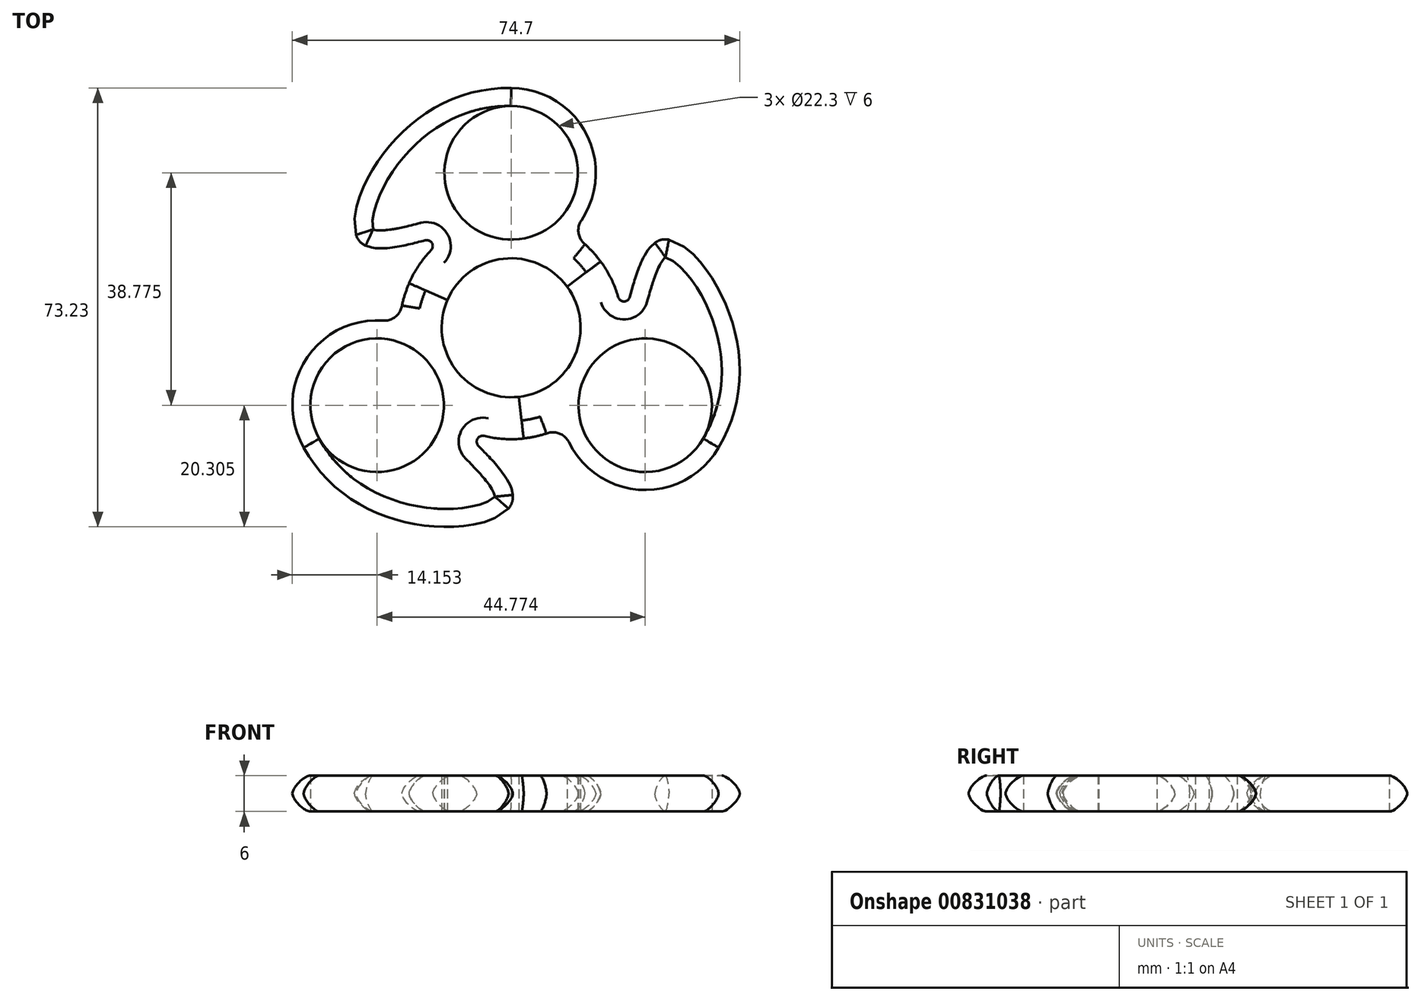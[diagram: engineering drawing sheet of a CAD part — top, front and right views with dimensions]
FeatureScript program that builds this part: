
annotation { "Feature Type Name" : "Feature", "Feature Type Description" : "" }
export const myFeature = defineFeature(function(context is Context, id is Id, definition is map)
    precondition{}
    {
        {
            var Q0;
            Q0=qCreatedBy(makeId("Top.planeOp"),FACE);
            var sketch = newSketch(context, id + "F0", { "sketchPlane" : qUnion([Q0])});
            skArc(sketch, "E0", {"start": v(9.33, 6.9) * mm, "mid": v(-1.3, 11.53) * mm, "end": v(-10.63, 4.64) * mm});
            skLineSegment(sketch, "E1", {"start": v(0, 0) * mm, "end": v(0, 40) * mm, "construction": true});
            skArc(sketch, "E2.0", {"start": v(-13.37, 12.93) * mm, "mid": v(-15.46, 10.35) * mm, "end": v(-17.05, 7.43) * mm});
            skArc(sketch, "E3.0", {"start": v(11.73, 17.94) * mm, "mid": v(12.5, 32.5) * mm, "end": v(0, 40) * mm});
            skLineSegment(sketch, "E4", {"start": v(0, 26.09) * mm, "end": v(14.15, 26.09) * mm, "construction": true});
            skArc(sketch, "E5", {"start": v(32.18, 23.76) * mm, "mid": v(-4.5, 39.75) * mm, "end": v(-36.67, 15.98) * mm, "construction": true});
            skArc(sketch, "E6", {"start": v(23.87, 17.63) * mm, "mid": v(-3.33, 29.49) * mm, "end": v(-27.2, 11.86) * mm, "construction": true});
            skFitSpline(sketch, "E7", {"points": [v(0, 40) * mm, v(-25.65, 14.92) * mm, v(-9.9, 15.74) * mm], "startDerivative": vector(-92.48, 1.82) * mm, "endDerivative": vector(44.55, 10.43) * mm});
            skCircle(sketch, "E8", {"center": v(0, 25.85) * mm, "radius": 11.15 * mm});
            skArc(sketch, "E9.filletArc", {"start": v(-13.37, 12.93) * mm, "mid": v(-13.22, 14.13) * mm, "end": v(-14.34, 14.6) * mm});
            skPoint(sketch, "E10.orphan", {"position": v(-18.59, 0.7) * mm});
            skPoint(sketch, "E11.orphan", {"position": v(8.68, -16.45) * mm});
            skPoint(sketch, "E12.visualSharp", {"position": v(9.9, 15.74) * mm});
            skArc(sketch, "E12.filletArc", {"start": v(11.73, 17.94) * mm, "mid": v(11.25, 15.82) * mm, "end": v(12.32, 13.93) * mm});
            skLineSegment(sketch, "E13", {"start": v(0, 0) * mm, "end": v(32.18, 23.76) * mm, "construction": true});
            skLineSegment(sketch, "E14", {"start": v(0, 0) * mm, "end": v(-36.67, 15.98) * mm, "construction": true});
            skPoint(sketch, "E15.orphan", {"position": v(-34.64, -20) * mm});
            skArc(sketch, "E16.trimOffspring", {"start": v(14.94, 11.03) * mm, "mid": v(13.71, 12.56) * mm, "end": v(12.32, 13.93) * mm});
            skPoint(sketch, "E17.orphan", {"position": v(34.64, -20) * mm});
            skLineSegment(sketch, "E18", {"start": v(-17.05, 7.43) * mm, "end": v(-10.63, 4.64) * mm});
            skLineSegment(sketch, "E19", {"start": v(9.33, 6.9) * mm, "end": v(14.94, 11.03) * mm});
            skSolve(sketch);
        }
        {
            var Q0;
            Q0=makeQuery(id+"F0.imprint","IMPRINT",FACE,{"disambiguationData":[TD([[makeQuery(id+"F0.imprint","IMPRINT",EDGE,{"derivedFrom":sQuery(id+"F0.wireOp",EDGE,"E0")}),-1.0]])]});
            extrude(context, id + "F1", {"entities" : qUnion([Q0]), "depth" : 6 * mm, "offsetDistance" : 25 * mm});
        }
        {
            var Q0;
            Q0=makeQuery(id+"F1.opExtrude","CAP_EDGE",EDGE,{"disambiguationData":[OSD([sQuery(id+"F0.wireOp",EDGE,"E2.0")])],"isStart":false});
            var Q1;
            Q1=makeQuery(id+"F1.opExtrude","CAP_EDGE",EDGE,{"disambiguationData":[OSD([sQuery(id+"F0.wireOp",EDGE,"E9.filletArc")])],"isStart":false});
            var Q2;
            Q2=makeQuery(id+"F1.opExtrude","CAP_EDGE",EDGE,{"disambiguationData":[OSD([sQuery(id+"F0.wireOp",EDGE,"E2.0")])],"isStart":true});
            var Q3;
            Q3=makeQuery(id+"F1.opExtrude","CAP_EDGE",EDGE,{"disambiguationData":[OSD([sQuery(id+"F0.wireOp",EDGE,"E3.0")])],"isStart":true});
            var Q4;
            Q4=makeQuery(id+"F1.opExtrude","CAP_EDGE",EDGE,{"disambiguationData":[OSD([sQuery(id+"F0.wireOp",EDGE,"E16.trimOffspring")])],"isStart":true});
            var Q5;
            Q5=makeQuery(id+"F1.opExtrude","CAP_EDGE",EDGE,{"disambiguationData":[OSD([sQuery(id+"F0.wireOp",EDGE,"E12.filletArc")])],"isStart":true});
            var Q6;
            Q6=makeQuery(id+"F1.opExtrude","CAP_EDGE",EDGE,{"disambiguationData":[OSD([sQuery(id+"F0.wireOp",EDGE,"E3.0")])],"isStart":false});
            var Q7;
            Q7=makeQuery(id+"F1.opExtrude","CAP_EDGE",EDGE,{"disambiguationData":[OSD([sQuery(id+"F0.wireOp",EDGE,"E12.filletArc")])],"isStart":false});
            var Q8;
            Q8=makeQuery(id+"F1.opExtrude","CAP_EDGE",EDGE,{"disambiguationData":[OSD([sQuery(id+"F0.wireOp",EDGE,"E16.trimOffspring")])],"isStart":false});
            var Q9;
            Q9=makeQuery(id+"F1.opExtrude","CAP_EDGE",EDGE,{"disambiguationData":[OSD([sQuery(id+"F0.wireOp",EDGE,"E9.filletArc")])],"isStart":true});
            fillet(context, id + "F2", {"entities" : qUnion([Q0, Q1, Q2, Q3, Q4, Q5, Q6, Q7, Q8, Q9]), "radius" : 3 * mm, "tangentPropagation" : true, "rho" : 0.25, "crossSection" : FilletCrossSection.CONIC, "allowEdgeOverflow" : false});
        }
        {
            var Q0;
            Q0=qCreatedBy(makeId("Front.planeOp"),FACE);
            var sketch = newSketch(context, id + "F3", { "sketchPlane" : qUnion([Q0])});
            skLineSegment(sketch, "E20", {"start": v(0, 0) * mm, "end": v(0, 13.93) * mm, "construction": true});
            skSolve(sketch);
        }
        {
            var Q0;
            Q0=makeQuery(id+"F1.opExtrude","SWEPT_BODY",BODY,{"disambiguationData":[OSD([sQuery(id+"F0.wireOp",EDGE,"E0"),sQuery(id+"F0.wireOp",EDGE,"E2.0"),sQuery(id+"F0.wireOp",EDGE,"E3.0"),sQuery(id+"F0.wireOp",EDGE,"E7"),sQuery(id+"F0.wireOp",EDGE,"E8"),sQuery(id+"F0.wireOp",EDGE,"E9.filletArc"),sQuery(id+"F0.wireOp",EDGE,"E12.filletArc"),sQuery(id+"F0.wireOp",EDGE,"E16.trimOffspring"),sQuery(id+"F0.wireOp",EDGE,"E18"),sQuery(id+"F0.wireOp",EDGE,"E19")])]});
            var Q1;
            Q1=sQuery(id+"F3.wireOp",EDGE,"E20");
            circularPattern(context, id + "F4", {"entities" : qUnion([Q0]), "axis" : qUnion([Q1]), "angle" : 360 * degree, "instanceCount" : 3, "equalSpace" : true});
        }
    });
